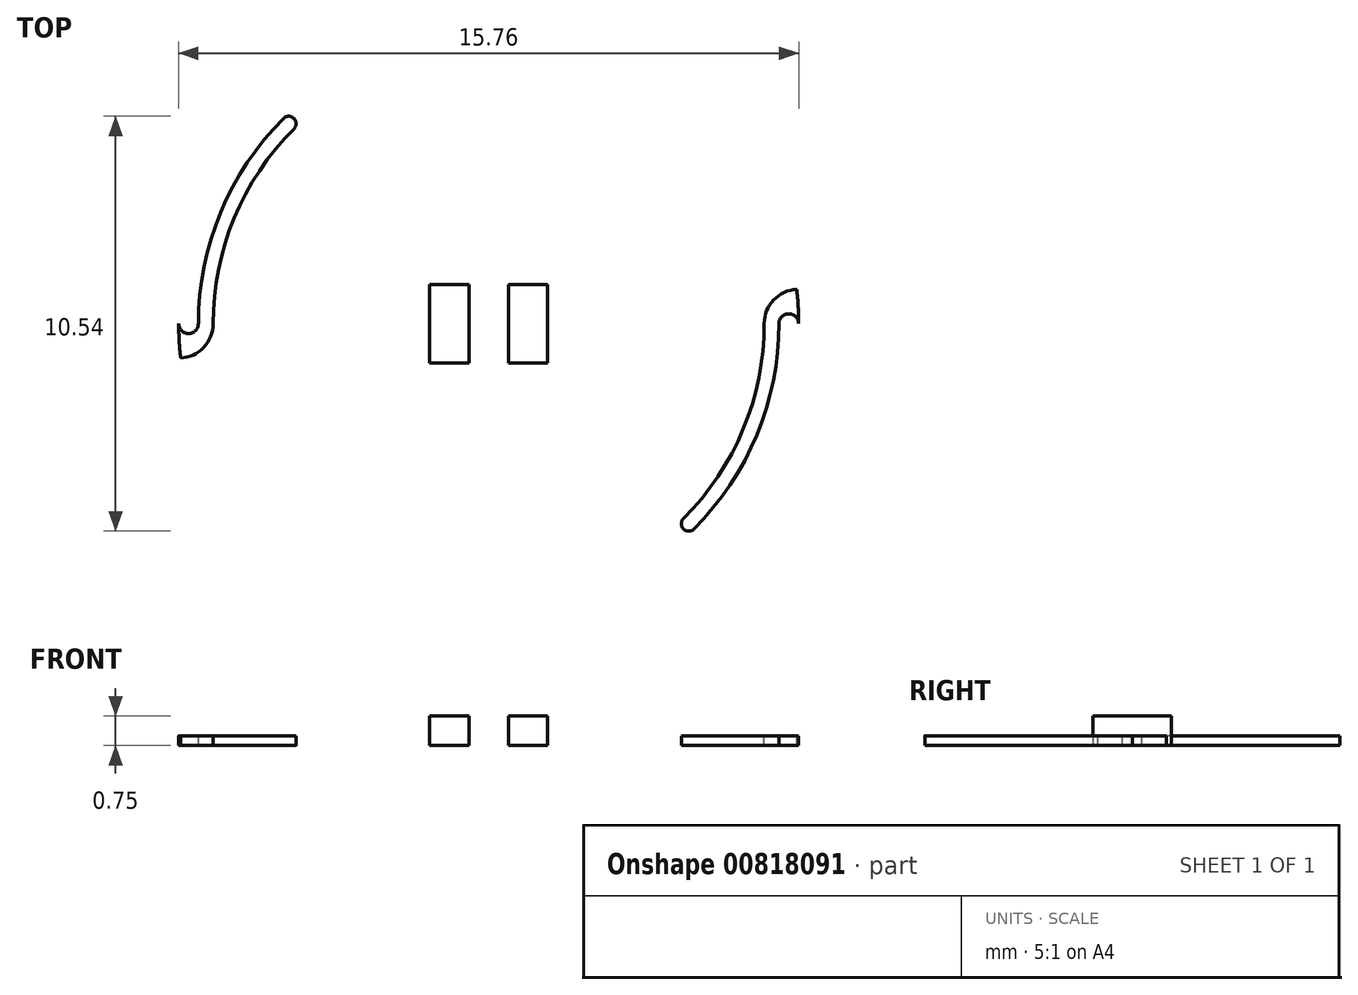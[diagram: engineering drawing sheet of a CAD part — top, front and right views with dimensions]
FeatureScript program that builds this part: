
annotation { "Feature Type Name" : "Feature", "Feature Type Description" : "" }
export const myFeature = defineFeature(function(context is Context, id is Id, definition is map)
    precondition{}
    {
        {
            var Q0;
            Q0=qCreatedBy(makeId("Top.planeOp"),FACE);
            var sketch = newSketch(context, id + "F0", { "sketchPlane" : qUnion([Q0])});
            skCircle(sketch, "E0", {"center": v(0, 0) * mm, "radius": 7.88 * mm});
            skSolve(sketch);
        }
        {
            var Q0;
            Q0=makeQuery(id+"F0.imprint","IMPRINT",FACE,{"disambiguationData":[TD([[makeQuery(id+"F0.imprint","IMPRINT",EDGE,{"derivedFrom":sQuery(id+"F0.wireOp",EDGE,"E0")}),1.0]])]});
            extrude(context, id + "F1", {"entities" : qUnion([Q0]), "depth" : 0.25 * mm, "offsetDistance" : 25 * mm});
        }
        {
            var Q0;
            Q0=makeQuery(id+"F1.opExtrude","CAP_FACE",FACE,{"disambiguationData":[OSD([sQuery(id+"F0.wireOp",EDGE,"E0")])],"isStart":false});
            var sketch = newSketch(context, id + "F2", { "sketchPlane" : qUnion([Q0])});
            skLineSegment(sketch, "E1.bottom", {"start": v(-1.5, 1) * mm, "end": v(-0.5, 1) * mm});
            skLineSegment(sketch, "E1.top", {"start": v(-1.5, -1) * mm, "end": v(-0.5, -1) * mm});
            skLineSegment(sketch, "E1.left", {"start": v(-1.5, 1) * mm, "end": v(-1.5, -1) * mm});
            skLineSegment(sketch, "E1.right", {"start": v(-0.5, 1) * mm, "end": v(-0.5, -1) * mm});
            skLineSegment(sketch, "E2", {"start": v(0.96, 0) * mm, "end": v(-1.5, 0) * mm, "construction": true});
            skLineSegment(sketch, "E3", {"start": v(0, -2.2) * mm, "end": v(0, -7.28) * mm, "construction": true});
            skLineSegment(sketch, "E4.MirrorCS", {"start": v(1.5, 1) * mm, "end": v(1.5, -1) * mm});
            skLineSegment(sketch, "E5.MirrorCS", {"start": v(0.5, 1) * mm, "end": v(0.5, -1) * mm});
            skLineSegment(sketch, "E6.MirrorCS", {"start": v(1.5, 1) * mm, "end": v(0.5, 1) * mm});
            skLineSegment(sketch, "E7.MirrorCS", {"start": v(1.5, -1) * mm, "end": v(0.5, -1) * mm});
            skSolve(sketch);
        }
        {
            var Q0;
            Q0=qSketchRegion(id+"F2",true);
            extrude(context, id + "F3", {"entities" : qUnion([Q0]), "operationType" : NewBodyOperationType.ADD, "depth" : 0.5 * mm, "offsetDistance" : 25 * mm});
        }
        {
            var Q0;
            Q0=makeQuery(id+"F1.opExtrude","CAP_FACE",FACE,{"disambiguationData":[OSD([sQuery(id+"F0.wireOp",EDGE,"E0")])],"isStart":false});
            var sketch = newSketch(context, id + "F4", { "sketchPlane" : qUnion([Q0])});
            skLineSegment(sketch, "E8.bottom", {"start": v(0.5, -8.88) * mm, "end": v(-0.5, -8.88) * mm});
            skLineSegment(sketch, "E8.top", {"start": v(0.25, -6.88) * mm, "end": v(-0.25, -6.88) * mm});
            skLineSegment(sketch, "E8.left", {"start": v(0.5, -8.88) * mm, "end": v(0.5, -7.12) * mm});
            skLineSegment(sketch, "E8.right", {"start": v(-0.5, -8.88) * mm, "end": v(-0.5, -7.12) * mm});
            skLineSegment(sketch, "E9", {"start": v(0, 16.81) * mm, "end": v(0, 8.88) * mm, "construction": true});
            skPoint(sketch, "E10.visualSharp", {"position": v(0.5, -6.88) * mm});
            skArc(sketch, "E10.filletArc", {"start": v(0.5, -7.12) * mm, "mid": v(0.43, -6.95) * mm, "end": v(0.25, -6.88) * mm});
            skPoint(sketch, "E11.visualSharp", {"position": v(-0.5, -6.88) * mm});
            skArc(sketch, "E11.filletArc", {"start": v(-0.25, -6.88) * mm, "mid": v(-0.43, -6.95) * mm, "end": v(-0.5, -7.12) * mm});
            skLineSegment(sketch, "E12", {"start": v(4.5, 0) * mm, "end": v(-2.65, 0) * mm, "construction": true});
            skSolve(sketch);
        }
        {
            var Q0;
            Q0=makeQuery(id+"F4.imprint","IMPRINT",FACE,{"disambiguationData":[TD([[makeQuery(id+"F4.imprint","IMPRINT",EDGE,{"derivedFrom":sQuery(id+"F4.wireOp",EDGE,"E8.top")}),1.0]])]});
            var Q1;
            {var subQ0=sQuery(id+"F4.wireOp",EDGE,"65e887c0-a7f7-40e5-952b-3a9e0b5064ee0.MirrorCS");Q1=makeQuery(id+"F4.imprint","IMPRINT",FACE,{"disambiguationData":[TD([[makeQuery(id+"F4.imprint","IMPRINT",EDGE,{"derivedFrom":subQ0}),-1.0]])]});}
            extrude(context, id + "F5", {"entities" : qUnion([Q0, Q1]), "operationType" : NewBodyOperationType.REMOVE, "oppositeDirection" : true, "depth" : 0.5 * mm, "offsetDistance" : 25 * mm});
        }
        {
            var Q0;
            Q0=makeQuery(id+"F1.opExtrude","CAP_FACE",FACE,{"disambiguationData":[OSD([sQuery(id+"F0.wireOp",EDGE,"E0")])],"isStart":false});
            var sketch = newSketch(context, id + "F6", { "sketchPlane" : qUnion([Q0])});
            skPoint(sketch, "E13.center", {"position": v(0, 0) * mm});
            skLineSegment(sketch, "E14", {"start": v(0, 4.02) * mm, "end": v(0, -4.13) * mm, "construction": true});
            skLineSegment(sketch, "E15.1.0", {"start": v(-1.54, 3.72) * mm, "end": v(1.58, -3.81) * mm, "construction": true});
            skLineSegment(sketch, "E15.2.0", {"start": v(-2.84, 2.84) * mm, "end": v(2.92, -2.92) * mm, "construction": true});
            skLineSegment(sketch, "E15.3.0", {"start": v(-3.72, 1.54) * mm, "end": v(3.81, -1.58) * mm, "construction": true});
            skLineSegment(sketch, "E15.4.0", {"start": v(-4.02, 0) * mm, "end": v(4.13, 0) * mm, "construction": true});
            skLineSegment(sketch, "E15.5.0", {"start": v(-3.72, -1.54) * mm, "end": v(3.81, 1.58) * mm, "construction": true});
            skLineSegment(sketch, "E15.6.0", {"start": v(-2.84, -2.84) * mm, "end": v(2.92, 2.92) * mm, "construction": true});
            skLineSegment(sketch, "E15.7.0", {"start": v(-1.54, -3.72) * mm, "end": v(1.58, 3.81) * mm, "construction": true});
            skLineSegment(sketch, "E15.8.0", {"start": v(0, -4.02) * mm, "end": v(0, 4.13) * mm, "construction": true});
            skLineSegment(sketch, "E15.9.0", {"start": v(1.54, -3.72) * mm, "end": v(-1.58, 3.81) * mm, "construction": true});
            skLineSegment(sketch, "E15.10.0", {"start": v(2.84, -2.84) * mm, "end": v(-2.92, 2.92) * mm, "construction": true});
            skLineSegment(sketch, "E15.11.0", {"start": v(3.72, -1.54) * mm, "end": v(-3.81, 1.58) * mm, "construction": true});
            skLineSegment(sketch, "E15.12.0", {"start": v(4.02, 0) * mm, "end": v(-4.13, 0) * mm, "construction": true});
            skLineSegment(sketch, "E15.13.0", {"start": v(3.72, 1.54) * mm, "end": v(-3.81, -1.58) * mm, "construction": true});
            skLineSegment(sketch, "E15.14.0", {"start": v(2.84, 2.84) * mm, "end": v(-2.92, -2.92) * mm, "construction": true});
            skLineSegment(sketch, "E15.15.0", {"start": v(1.54, 3.72) * mm, "end": v(-1.58, -3.81) * mm, "construction": true});
            skArc(sketch, "E16", {"start": v(-7.38, 0) * mm, "mid": v(-6.81, 2.82) * mm, "end": v(-5.21, 5.21) * mm});
            skArc(sketch, "E17", {"start": v(-7, 0) * mm, "mid": v(-6.47, 2.68) * mm, "end": v(-4.95, 4.95) * mm});
            skArc(sketch, "E18", {"start": v(-7.37, 0) * mm, "mid": v(-7.62, -0.25) * mm, "end": v(-7.88, 0) * mm});
            skArc(sketch, "E19", {"start": v(-4.95, 4.95) * mm, "mid": v(-4.95, 5.21) * mm, "end": v(-5.21, 5.21) * mm});
            skArc(sketch, "E20", {"start": v(-7, 0) * mm, "mid": v(-7.24, -0.6) * mm, "end": v(-7.83, -0.87) * mm});
            skArc(sketch, "E21", {"start": v(-7.83, -0.87) * mm, "mid": v(-8.29, -0.46) * mm, "end": v(-7.88, 0) * mm});
            skArc(sketch, "E22.1.1", {"start": v(7, 0) * mm, "mid": v(6.47, -2.68) * mm, "end": v(4.95, -4.95) * mm});
            skArc(sketch, "E22.1.2", {"start": v(7.38, 0) * mm, "mid": v(6.81, -2.82) * mm, "end": v(5.21, -5.21) * mm});
            skArc(sketch, "E22.1.3", {"start": v(4.95, -4.95) * mm, "mid": v(4.95, -5.21) * mm, "end": v(5.21, -5.21) * mm});
            skArc(sketch, "E22.1.4", {"start": v(7.83, 0.87) * mm, "mid": v(8.29, 0.46) * mm, "end": v(7.88, 0) * mm});
            skArc(sketch, "E22.1.5", {"start": v(7, 0) * mm, "mid": v(7.24, 0.6) * mm, "end": v(7.83, 0.87) * mm});
            skArc(sketch, "E22.1.6", {"start": v(7.37, 0) * mm, "mid": v(7.62, 0.25) * mm, "end": v(7.88, 0) * mm});
            skSolve(sketch);
        }
        {
            var Q0;
            Q0=makeQuery(id+"F6.imprint","IMPRINT",FACE,{"disambiguationData":[TD([[makeQuery(id+"F6.imprint","IMPRINT",EDGE,{"derivedFrom":sQuery(id+"F6.wireOp",EDGE,"E16")}),-1.0]])]});
            var Q1;
            Q1=makeQuery(id+"F6.imprint","IMPRINT",FACE,{"disambiguationData":[TD([[makeQuery(id+"F6.imprint","IMPRINT",EDGE,{"derivedFrom":sQuery(id+"F6.wireOp",EDGE,"E22.1.1")}),1.0]])]});
            extrude(context, id + "F7", {"entities" : qUnion([Q0, Q1]), "operationType" : NewBodyOperationType.REMOVE, "oppositeDirection" : true, "depth" : 1 * mm, "offsetDistance" : 25 * mm});
        }
    });
